# Revit family: C-76-EB_RFA
name_source: partatom
category: Aparatos sanitarios
units: mm (PartAtom-declared; Revit-internal decimal feet)

## family parameters
Activar corte en vistas = No
Anfitrión = Cara
Compartido = Sí
Corte con vacíos al cargar = No
Cota de conector redondo = Usar diámetro
Mantener orientación de anotación = No
Número OmniClass = 23.45.00.00
Punto de cálculo de habitación = Sí
Tipo de pieza = Normal
Título OmniClass = Sanitary, Laundry, and Cleaning Equipment

## types (1)
- C-76-EB
    Accesorios = Llave Allen 5/64"
    Ancho = 2.5 "
    Comentarios de tipo = Juego de Manerales Cuadrados
    Cromo = Cromo
    Descripción = Juego de manerales cuadrados para ensambles de
taladros separados para lavabo, bidet, fregadero y
emsambles de empotrar de lavabo, regadera y/o
tina.
    Elevación por defecto = 48 "
    Fabricante = HELVEX S.A. DE C.V.
    Garantía = El producto HELVEX está garantizado como
libre de defectos en materiales, mano de obra y
procesos de fabricación.
El producto HELVEX está garantizado,en lo que
se refiere a los acabados, por 10 años para los
acabados Cromo y Duravex, y por 2 años en
acabados diferentes al Cromo y Duravex.
Las piezas que sufren desgaste natural en el
producto están garantizadas para uso
residencial por 5 años, y para uso comercial por
3 años.
La vigencia de la garantía inicia a partir de la
fecha de entrega del producto al consumidor
indicada en la Póliza de Garantía.
    Imagen de tipo = C-76.png
    Largo = 2.5 "
    Modelo = C-76-EB
    Operación = Compatible con Valvex V con giro de 1/4 de vuelta.
Compatible con Valvex I con giro de vuelta
completa.
    Profundidad = 2.41 "
    Ébano = Ébano

## geometry (parser evidence)
native form markers: Sweep x7
no freeform markers — native parametric forms only
